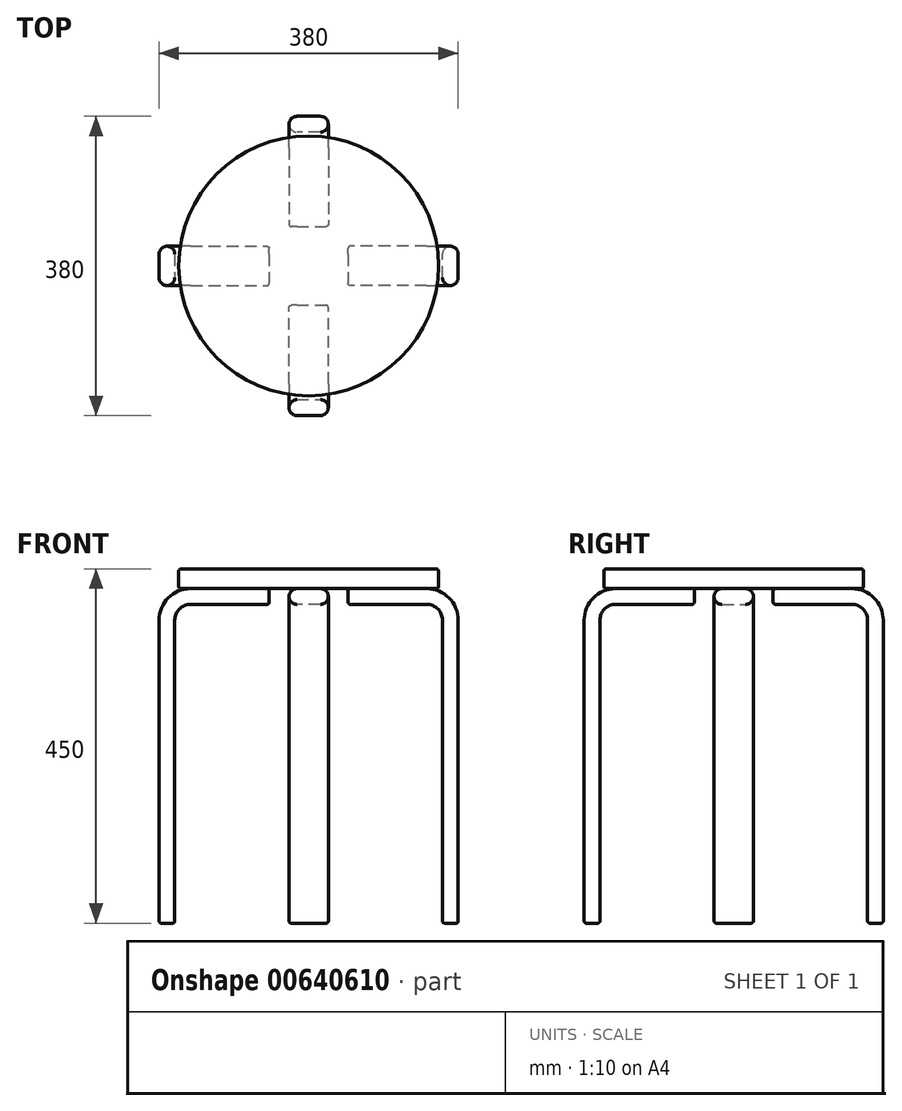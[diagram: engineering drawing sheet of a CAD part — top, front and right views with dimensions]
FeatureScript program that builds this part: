
annotation { "Feature Type Name" : "Feature", "Feature Type Description" : "" }
export const myFeature = defineFeature(function(context is Context, id is Id, definition is map)
    precondition{}
    {
        {
            var Q0;
            Q0=qCreatedBy(makeId("Top.planeOp"),FACE);
            var sketch = newSketch(context, id + "F0", { "sketchPlane" : qUnion([Q0])});
            skLineSegment(sketch, "E0", {"start": v(0, 0) * mm, "end": v(-180, 0) * mm, "construction": true});
            skLineSegment(sketch, "E1", {"start": v(-180, -15) * mm, "end": v(-180, 15) * mm, "construction": true});
            skArc(sketch, "E2", {"start": v(-170, 15) * mm, "mid": v(-180, 25) * mm, "end": v(-190, 15) * mm});
            skArc(sketch, "E3", {"start": v(-190, -15) * mm, "mid": v(-180, -25) * mm, "end": v(-170, -15) * mm});
            skLineSegment(sketch, "E4", {"start": v(-180, 15) * mm, "end": v(-170, 15) * mm, "construction": true});
            skLineSegment(sketch, "E5", {"start": v(-190, 15) * mm, "end": v(-190, -15) * mm});
            skLineSegment(sketch, "E6", {"start": v(-170, 15) * mm, "end": v(-170, -15) * mm});
            skSolve(sketch);
        }
        {
            var Q0;
            Q0=qCreatedBy(makeId("Front.planeOp"),FACE);
            var sketch = newSketch(context, id + "F1", { "sketchPlane" : qUnion([Q0])});
            skLineSegment(sketch, "E7", {"start": v(-180, 0) * mm, "end": v(-180, 385) * mm});
            skLineSegment(sketch, "E8", {"start": v(-50, 415) * mm, "end": v(-150, 415) * mm});
            skPoint(sketch, "E9.visualSharp", {"position": v(-180, 415) * mm});
            skArc(sketch, "E9.filletArc", {"start": v(-150, 415) * mm, "mid": v(-171.21, 406.21) * mm, "end": v(-180, 385) * mm});
            skSolve(sketch);
        }
        {
            var Q0;
            Q0=makeQuery(id+"F0.imprint","IMPRINT",FACE,{"disambiguationData":[TD([[makeQuery(id+"F0.imprint","IMPRINT",EDGE,{"derivedFrom":sQuery(id+"F0.wireOp",EDGE,"E2")}),1.0]])]});
            var Q1;
            Q1=sQuery(id+"F1.wireOp",EDGE,"E7");
            var Q2;
            Q2=sQuery(id+"F1.wireOp",EDGE,"E9.filletArc");
            var Q3;
            Q3=sQuery(id+"F1.wireOp",EDGE,"E8");
            sweep(context, id + "F2", {"profiles" : qUnion([Q0]), "path" : qUnion([Q1, Q2, Q3])});
        }
        {
            var Q0;
            Q0=qCreatedBy(makeId("Front.planeOp"),FACE);
            var sketch = newSketch(context, id + "F3", { "sketchPlane" : qUnion([Q0])});
            skLineSegment(sketch, "E10", {"start": v(0, 0) * mm, "end": v(0, 83.06) * mm, "construction": true});
            skSolve(sketch);
        }
        {
            var Q0;
            Q0=makeQuery(id+"F2.opSweep","SWEPT_BODY",BODY,{"disambiguationData":[OSD([sQuery(id+"F0.wireOp",EDGE,"E2"),sQuery(id+"F0.wireOp",EDGE,"E3"),sQuery(id+"F0.wireOp",EDGE,"E5"),sQuery(id+"F0.wireOp",EDGE,"E6"),sQuery(id+"F1.wireOp",EDGE,"E8")])]});
            var Q1;
            Q1=sQuery(id+"F3.wireOp",EDGE,"E10");
            circularPattern(context, id + "F4", {"entities" : qUnion([Q0]), "axis" : qUnion([Q1]), "angle" : 360 * degree, "instanceCount" : 4, "equalSpace" : true});
        }
        {
            var Q0;
            Q0=qCreatedBy(makeId("Front.planeOp"),FACE);
            var sketch = newSketch(context, id + "F5", { "sketchPlane" : qUnion([Q0])});
            skLineSegment(sketch, "E11.bottom", {"start": v(-165, 450) * mm, "end": v(0, 450) * mm});
            skLineSegment(sketch, "E11.top", {"start": v(-165, 425) * mm, "end": v(0, 425) * mm});
            skLineSegment(sketch, "E11.left", {"start": v(-165, 450) * mm, "end": v(-165, 425) * mm});
            skLineSegment(sketch, "E11.right", {"start": v(0, 450) * mm, "end": v(0, 425) * mm});
            skSolve(sketch);
        }
        {
            var Q0;
            Q0=makeQuery(id+"F5.imprint","IMPRINT",FACE,{"disambiguationData":[TD([[makeQuery(id+"F5.imprint","IMPRINT",EDGE,{"derivedFrom":sQuery(id+"F5.wireOp",EDGE,"E11.bottom")}),-1.0]])]});
            var Q1;
            Q1=sQuery(id+"F3.wireOp",EDGE,"E10");
            revolve(context, id + "F6", {"entities" : qUnion([Q0]), "axis" : qUnion([Q1]), "revolveType" : RevolveType.FULL});
        }
        {
            var Q0;
            Q0=makeQuery(id+"F6.opRevolve","SWEPT_FACE",FACE,{"disambiguationData":[OSD([sQuery(id+"F5.wireOp",EDGE,"E11.left")])]});
            var Q1;
            Q1=makeQuery(id+"F6.opRevolve","SWEPT_EDGE",EDGE,{"disambiguationData":[OSD([sQuery(id+"F5.wireOp",EDGE,"E11.top"),sQuery(id+"F5.wireOp",EDGE,"E11.left")])]});
            var Q2;
            Q2=makeQuery(id+"F6.opRevolve","SWEPT_EDGE",EDGE,{"disambiguationData":[OSD([sQuery(id+"F5.wireOp",EDGE,"E11.bottom"),sQuery(id+"F5.wireOp",EDGE,"E11.left")])]});
            var Q3;
            Q3=makeQuery(id+"F6.opRevolve","SWEPT_FACE",FACE,{"disambiguationData":[OSD([sQuery(id+"F5.wireOp",EDGE,"E11.top")])]});
            var Q4;
            Q4=makeQuery(id+"F6.opRevolve","SWEPT_FACE",FACE,{"disambiguationData":[OSD([sQuery(id+"F5.wireOp",EDGE,"E11.bottom")])]});
            var Q5;
            Q5=makeQuery(id+"F4.opPattern","COPY",FACE,{"derivedFrom":makeQuery(id+"F2.opSweep","SWEPT_FACE",FACE,{"disambiguationData":[OSD([sQuery(id+"F0.wireOp",EDGE,"E2"),sQuery(id+"F1.wireOp",EDGE,"E7")])]}),"instanceName":"3"});
            var Q6;
            Q6=makeQuery(id+"F4.opPattern","COPY",FACE,{"derivedFrom":makeQuery(id+"F2.opSweep","SWEPT_FACE",FACE,{"disambiguationData":[OSD([sQuery(id+"F0.wireOp",EDGE,"E3"),sQuery(id+"F1.wireOp",EDGE,"E7")])]}),"instanceName":"3"});
            var Q7;
            Q7=makeQuery(id+"F4.opPattern","COPY",FACE,{"derivedFrom":makeQuery(id+"F2.opSweep","SWEPT_FACE",FACE,{"disambiguationData":[OSD([sQuery(id+"F0.wireOp",EDGE,"E6"),sQuery(id+"F1.wireOp",EDGE,"E7")])]}),"instanceName":"3"});
            var Q8;
            Q8=makeQuery(id+"F4.opPattern","COPY",FACE,{"derivedFrom":makeQuery(id+"F2.opSweep","CAP_FACE",FACE,{"disambiguationData":[OSD([sQuery(id+"F0.wireOp",EDGE,"E2"),sQuery(id+"F0.wireOp",EDGE,"E3"),sQuery(id+"F0.wireOp",EDGE,"E5"),sQuery(id+"F0.wireOp",EDGE,"E6"),sQuery(id+"F1.wireOp",VERTEX,"E7.start")])],"isStart":true}),"instanceName":"3"});
            var Q9;
            Q9=makeQuery(id+"F4.opPattern","COPY",FACE,{"derivedFrom":makeQuery(id+"F2.opSweep","SWEPT_FACE",FACE,{"disambiguationData":[OSD([sQuery(id+"F0.wireOp",EDGE,"E5"),sQuery(id+"F1.wireOp",EDGE,"E7")])]}),"instanceName":"1"});
            var Q10;
            Q10=makeQuery(id+"F4.opPattern","COPY",FACE,{"derivedFrom":makeQuery(id+"F2.opSweep","SWEPT_FACE",FACE,{"disambiguationData":[OSD([sQuery(id+"F0.wireOp",EDGE,"E3"),sQuery(id+"F1.wireOp",EDGE,"E9.filletArc")])]}),"instanceName":"1"});
            var Q11;
            Q11=makeQuery(id+"F4.opPattern","COPY",FACE,{"derivedFrom":makeQuery(id+"F2.opSweep","SWEPT_FACE",FACE,{"disambiguationData":[OSD([sQuery(id+"F0.wireOp",EDGE,"E3"),sQuery(id+"F1.wireOp",EDGE,"E8")])]}),"instanceName":"1"});
            var Q12;
            Q12=makeQuery(id+"F4.opPattern","COPY",FACE,{"derivedFrom":makeQuery(id+"F2.opSweep","SWEPT_FACE",FACE,{"disambiguationData":[OSD([sQuery(id+"F0.wireOp",EDGE,"E3"),sQuery(id+"F1.wireOp",EDGE,"E7")])]}),"instanceName":"1"});
            var Q13;
            Q13=makeQuery(id+"F4.opPattern","COPY",FACE,{"derivedFrom":makeQuery(id+"F2.opSweep","SWEPT_FACE",FACE,{"disambiguationData":[OSD([sQuery(id+"F0.wireOp",EDGE,"E2"),sQuery(id+"F1.wireOp",EDGE,"E9.filletArc")])]}),"instanceName":"1"});
            var Q14;
            Q14=makeQuery(id+"F4.opPattern","COPY",FACE,{"derivedFrom":makeQuery(id+"F2.opSweep","SWEPT_FACE",FACE,{"disambiguationData":[OSD([sQuery(id+"F0.wireOp",EDGE,"E2"),sQuery(id+"F1.wireOp",EDGE,"E7")])]}),"instanceName":"1"});
            var Q15;
            Q15=makeQuery(id+"F4.opPattern","COPY",FACE,{"derivedFrom":makeQuery(id+"F2.opSweep","CAP_FACE",FACE,{"disambiguationData":[OSD([sQuery(id+"F0.wireOp",EDGE,"E2"),sQuery(id+"F0.wireOp",EDGE,"E3"),sQuery(id+"F0.wireOp",EDGE,"E5"),sQuery(id+"F0.wireOp",EDGE,"E6"),sQuery(id+"F1.wireOp",VERTEX,"E8.start")])],"isStart":false}),"instanceName":"1"});
            var Q16;
            Q16=makeQuery(id+"F4.opPattern","COPY",FACE,{"derivedFrom":makeQuery(id+"F2.opSweep","CAP_FACE",FACE,{"disambiguationData":[OSD([sQuery(id+"F0.wireOp",EDGE,"E2"),sQuery(id+"F0.wireOp",EDGE,"E3"),sQuery(id+"F0.wireOp",EDGE,"E5"),sQuery(id+"F0.wireOp",EDGE,"E6"),sQuery(id+"F1.wireOp",VERTEX,"E7.start")])],"isStart":true}),"instanceName":"1"});
            var Q17;
            Q17=makeQuery(id+"F4.opPattern","COPY",FACE,{"derivedFrom":makeQuery(id+"F2.opSweep","SWEPT_FACE",FACE,{"disambiguationData":[OSD([sQuery(id+"F0.wireOp",EDGE,"E5"),sQuery(id+"F1.wireOp",EDGE,"E9.filletArc")])]}),"instanceName":"1"});
            var Q18;
            Q18=makeQuery(id+"F4.opPattern","COPY",EDGE,{"derivedFrom":makeQuery(id+"F2.opSweep","CAP_EDGE",EDGE,{"disambiguationData":[OSD([sQuery(id+"F0.wireOp",EDGE,"E5"),sQuery(id+"F1.wireOp",VERTEX,"E7.start")])],"isStart":true}),"instanceName":"1"});
            var Q19;
            Q19=makeQuery(id+"F4.opPattern","COPY",FACE,{"derivedFrom":makeQuery(id+"F2.opSweep","CAP_FACE",FACE,{"disambiguationData":[OSD([sQuery(id+"F0.wireOp",EDGE,"E2"),sQuery(id+"F0.wireOp",EDGE,"E3"),sQuery(id+"F0.wireOp",EDGE,"E5"),sQuery(id+"F0.wireOp",EDGE,"E6"),sQuery(id+"F1.wireOp",VERTEX,"E8.start")])],"isStart":false}),"instanceName":"2"});
            var Q20;
            Q20=makeQuery(id+"F4.opPattern","COPY",FACE,{"derivedFrom":makeQuery(id+"F2.opSweep","CAP_FACE",FACE,{"disambiguationData":[OSD([sQuery(id+"F0.wireOp",EDGE,"E2"),sQuery(id+"F0.wireOp",EDGE,"E3"),sQuery(id+"F0.wireOp",EDGE,"E5"),sQuery(id+"F0.wireOp",EDGE,"E6"),sQuery(id+"F1.wireOp",VERTEX,"E7.start")])],"isStart":true}),"instanceName":"2"});
            var Q21;
            Q21=makeQuery(id+"F4.opPattern","COPY",FACE,{"derivedFrom":makeQuery(id+"F2.opSweep","SWEPT_FACE",FACE,{"disambiguationData":[OSD([sQuery(id+"F0.wireOp",EDGE,"E2"),sQuery(id+"F1.wireOp",EDGE,"E7")])]}),"instanceName":"2"});
            var Q22;
            Q22=makeQuery(id+"F4.opPattern","COPY",EDGE,{"derivedFrom":makeQuery(id+"F2.opSweep","SWEPT_EDGE",EDGE,{"disambiguationData":[OSD([sQuery(id+"F0.wireOp",EDGE,"E2"),sQuery(id+"F0.wireOp",EDGE,"E5"),sQuery(id+"F1.wireOp",EDGE,"E9.filletArc")])]}),"instanceName":"2"});
            var Q23;
            Q23=makeQuery(id+"F4.opPattern","COPY",FACE,{"derivedFrom":makeQuery(id+"F2.opSweep","SWEPT_FACE",FACE,{"disambiguationData":[OSD([sQuery(id+"F0.wireOp",EDGE,"E2"),sQuery(id+"F1.wireOp",EDGE,"E8")])]}),"instanceName":"2"});
            var Q24;
            Q24=makeQuery(id+"F4.opPattern","COPY",FACE,{"derivedFrom":makeQuery(id+"F2.opSweep","SWEPT_FACE",FACE,{"disambiguationData":[OSD([sQuery(id+"F0.wireOp",EDGE,"E2"),sQuery(id+"F1.wireOp",EDGE,"E9.filletArc")])]}),"instanceName":"2"});
            var Q25;
            Q25=makeQuery(id+"F4.opPattern","COPY",EDGE,{"derivedFrom":makeQuery(id+"F2.opSweep","MID_CAP_EDGE",EDGE,{"disambiguationData":[OSD([sQuery(id+"F0.wireOp",EDGE,"E5"),sQuery(id+"F1.wireOp",VERTEX,"E9.filletArc.end")])],"capPos":1.0}),"instanceName":"2"});
            var Q26;
            Q26=makeQuery(id+"F4.opPattern","COPY",FACE,{"derivedFrom":makeQuery(id+"F2.opSweep","SWEPT_FACE",FACE,{"disambiguationData":[OSD([sQuery(id+"F0.wireOp",EDGE,"E3"),sQuery(id+"F1.wireOp",EDGE,"E7")])]}),"instanceName":"2"});
            var Q27;
            Q27=makeQuery(id+"F4.opPattern","COPY",EDGE,{"derivedFrom":makeQuery(id+"F2.opSweep","SWEPT_EDGE",EDGE,{"disambiguationData":[OSD([sQuery(id+"F0.wireOp",EDGE,"E3"),sQuery(id+"F0.wireOp",EDGE,"E5"),sQuery(id+"F1.wireOp",EDGE,"E9.filletArc")])]}),"instanceName":"2"});
            var Q28;
            Q28=makeQuery(id+"F4.opPattern","COPY",FACE,{"derivedFrom":makeQuery(id+"F2.opSweep","SWEPT_FACE",FACE,{"disambiguationData":[OSD([sQuery(id+"F0.wireOp",EDGE,"E3"),sQuery(id+"F1.wireOp",EDGE,"E9.filletArc")])]}),"instanceName":"2"});
            var Q29;
            Q29=makeQuery(id+"F4.opPattern","COPY",FACE,{"derivedFrom":makeQuery(id+"F2.opSweep","SWEPT_FACE",FACE,{"disambiguationData":[OSD([sQuery(id+"F0.wireOp",EDGE,"E5"),sQuery(id+"F1.wireOp",EDGE,"E7")])]}),"instanceName":"2"});
            var Q30;
            Q30=makeQuery(id+"F4.opPattern","COPY",FACE,{"derivedFrom":makeQuery(id+"F2.opSweep","SWEPT_FACE",FACE,{"disambiguationData":[OSD([sQuery(id+"F0.wireOp",EDGE,"E5"),sQuery(id+"F1.wireOp",EDGE,"E9.filletArc")])]}),"instanceName":"2"});
            var Q31;
            Q31=makeQuery(id+"F2.opSweep","SWEPT_FACE",FACE,{"disambiguationData":[OSD([sQuery(id+"F0.wireOp",EDGE,"E3"),sQuery(id+"F1.wireOp",EDGE,"E8")])]});
            var Q32;
            Q32=makeQuery(id+"F2.opSweep","SWEPT_FACE",FACE,{"disambiguationData":[OSD([sQuery(id+"F0.wireOp",EDGE,"E2"),sQuery(id+"F1.wireOp",EDGE,"E7")])]});
            var Q33;
            Q33=makeQuery(id+"F2.opSweep","SWEPT_FACE",FACE,{"disambiguationData":[OSD([sQuery(id+"F0.wireOp",EDGE,"E3"),sQuery(id+"F1.wireOp",EDGE,"E9.filletArc")])]});
            var Q34;
            Q34=makeQuery(id+"F2.opSweep","CAP_FACE",FACE,{"disambiguationData":[OSD([sQuery(id+"F0.wireOp",EDGE,"E2"),sQuery(id+"F0.wireOp",EDGE,"E3"),sQuery(id+"F0.wireOp",EDGE,"E5"),sQuery(id+"F0.wireOp",EDGE,"E6"),sQuery(id+"F1.wireOp",VERTEX,"E7.start")])],"isStart":true});
            var Q35;
            Q35=makeQuery(id+"F2.opSweep","SWEPT_FACE",FACE,{"disambiguationData":[OSD([sQuery(id+"F0.wireOp",EDGE,"E3"),sQuery(id+"F1.wireOp",EDGE,"E7")])]});
            var Q36;
            Q36=makeQuery(id+"F2.opSweep","SWEPT_EDGE",EDGE,{"disambiguationData":[OSD([sQuery(id+"F0.wireOp",EDGE,"E2"),sQuery(id+"F0.wireOp",EDGE,"E6"),sQuery(id+"F1.wireOp",EDGE,"E7")])]});
            var Q37;
            Q37=makeQuery(id+"F2.opSweep","SWEPT_FACE",FACE,{"disambiguationData":[OSD([sQuery(id+"F0.wireOp",EDGE,"E6"),sQuery(id+"F1.wireOp",EDGE,"E9.filletArc")])]});
            var Q38;
            Q38=makeQuery(id+"F2.opSweep","SWEPT_EDGE",EDGE,{"disambiguationData":[OSD([sQuery(id+"F0.wireOp",EDGE,"E3"),sQuery(id+"F0.wireOp",EDGE,"E6"),sQuery(id+"F1.wireOp",EDGE,"E7")])]});
            var Q39;
            Q39=makeQuery(id+"F2.opSweep","SWEPT_FACE",FACE,{"disambiguationData":[OSD([sQuery(id+"F0.wireOp",EDGE,"E6"),sQuery(id+"F1.wireOp",EDGE,"E7")])]});
            var Q40;
            Q40=makeQuery(id+"F4.opPattern","COPY",FACE,{"derivedFrom":makeQuery(id+"F2.opSweep","SWEPT_FACE",FACE,{"disambiguationData":[OSD([sQuery(id+"F0.wireOp",EDGE,"E2"),sQuery(id+"F1.wireOp",EDGE,"E8")])]}),"instanceName":"3"});
            var Q41;
            Q41=makeQuery(id+"F4.opPattern","COPY",EDGE,{"derivedFrom":makeQuery(id+"F2.opSweep","CAP_EDGE",EDGE,{"disambiguationData":[OSD([sQuery(id+"F0.wireOp",EDGE,"E5"),sQuery(id+"F1.wireOp",VERTEX,"E8.start")])],"isStart":false}),"instanceName":"3"});
            var Q42;
            Q42=makeQuery(id+"F4.opPattern","COPY",FACE,{"derivedFrom":makeQuery(id+"F2.opSweep","CAP_FACE",FACE,{"disambiguationData":[OSD([sQuery(id+"F0.wireOp",EDGE,"E2"),sQuery(id+"F0.wireOp",EDGE,"E3"),sQuery(id+"F0.wireOp",EDGE,"E5"),sQuery(id+"F0.wireOp",EDGE,"E6"),sQuery(id+"F1.wireOp",VERTEX,"E8.start")])],"isStart":false}),"instanceName":"3"});
            var Q43;
            Q43=makeQuery(id+"F4.opPattern","COPY",EDGE,{"derivedFrom":makeQuery(id+"F2.opSweep","CAP_EDGE",EDGE,{"disambiguationData":[OSD([sQuery(id+"F0.wireOp",EDGE,"E6"),sQuery(id+"F1.wireOp",VERTEX,"E7.start")])],"isStart":true}),"instanceName":"3"});
            var Q44;
            Q44=makeQuery(id+"F4.opPattern","COPY",FACE,{"derivedFrom":makeQuery(id+"F2.opSweep","SWEPT_FACE",FACE,{"disambiguationData":[OSD([sQuery(id+"F0.wireOp",EDGE,"E2"),sQuery(id+"F1.wireOp",EDGE,"E9.filletArc")])]}),"instanceName":"3"});
            var Q45;
            Q45=makeQuery(id+"F4.opPattern","COPY",EDGE,{"derivedFrom":makeQuery(id+"F2.opSweep","SWEPT_EDGE",EDGE,{"disambiguationData":[OSD([sQuery(id+"F0.wireOp",EDGE,"E3"),sQuery(id+"F0.wireOp",EDGE,"E6"),sQuery(id+"F1.wireOp",EDGE,"E7")])]}),"instanceName":"3"});
            var Q46;
            Q46=makeQuery(id+"F4.opPattern","COPY",FACE,{"derivedFrom":makeQuery(id+"F2.opSweep","SWEPT_FACE",FACE,{"disambiguationData":[OSD([sQuery(id+"F0.wireOp",EDGE,"E3"),sQuery(id+"F1.wireOp",EDGE,"E8")])]}),"instanceName":"3"});
            var Q47;
            Q47=makeQuery(id+"F4.opPattern","COPY",EDGE,{"derivedFrom":makeQuery(id+"F2.opSweep","CAP_EDGE",EDGE,{"disambiguationData":[OSD([sQuery(id+"F0.wireOp",EDGE,"E2"),sQuery(id+"F1.wireOp",VERTEX,"E7.start")])],"isStart":true}),"instanceName":"3"});
            var Q48;
            Q48=makeQuery(id+"F4.opPattern","COPY",FACE,{"derivedFrom":makeQuery(id+"F2.opSweep","SWEPT_FACE",FACE,{"disambiguationData":[OSD([sQuery(id+"F0.wireOp",EDGE,"E5"),sQuery(id+"F1.wireOp",EDGE,"E7")])]}),"instanceName":"3"});
            var Q49;
            Q49=makeQuery(id+"F4.opPattern","COPY",FACE,{"derivedFrom":makeQuery(id+"F2.opSweep","SWEPT_FACE",FACE,{"disambiguationData":[OSD([sQuery(id+"F0.wireOp",EDGE,"E5"),sQuery(id+"F1.wireOp",EDGE,"E8")])]}),"instanceName":"3"});
            var Q50;
            Q50=makeQuery(id+"F4.opPattern","COPY",FACE,{"derivedFrom":makeQuery(id+"F2.opSweep","SWEPT_FACE",FACE,{"disambiguationData":[OSD([sQuery(id+"F0.wireOp",EDGE,"E5"),sQuery(id+"F1.wireOp",EDGE,"E9.filletArc")])]}),"instanceName":"3"});
            var Q51;
            Q51=makeQuery(id+"F4.opPattern","COPY",EDGE,{"derivedFrom":makeQuery(id+"F2.opSweep","SWEPT_EDGE",EDGE,{"disambiguationData":[OSD([sQuery(id+"F0.wireOp",EDGE,"E2"),sQuery(id+"F0.wireOp",EDGE,"E6"),sQuery(id+"F1.wireOp",EDGE,"E7")])]}),"instanceName":"3"});
            var Q52;
            Q52=makeQuery(id+"F4.opPattern","COPY",EDGE,{"derivedFrom":makeQuery(id+"F2.opSweep","CAP_EDGE",EDGE,{"disambiguationData":[OSD([sQuery(id+"F0.wireOp",EDGE,"E3"),sQuery(id+"F1.wireOp",VERTEX,"E7.start")])],"isStart":true}),"instanceName":"3"});
            var Q53;
            Q53=makeQuery(id+"F4.opPattern","COPY",FACE,{"derivedFrom":makeQuery(id+"F2.opSweep","SWEPT_FACE",FACE,{"disambiguationData":[OSD([sQuery(id+"F0.wireOp",EDGE,"E6"),sQuery(id+"F1.wireOp",EDGE,"E8")])]}),"instanceName":"3"});
            var Q54;
            Q54=makeQuery(id+"F4.opPattern","COPY",EDGE,{"derivedFrom":makeQuery(id+"F2.opSweep","CAP_EDGE",EDGE,{"disambiguationData":[OSD([sQuery(id+"F0.wireOp",EDGE,"E5"),sQuery(id+"F1.wireOp",VERTEX,"E7.start")])],"isStart":true}),"instanceName":"3"});
            var Q55;
            Q55=makeQuery(id+"F4.opPattern","COPY",EDGE,{"derivedFrom":makeQuery(id+"F2.opSweep","SWEPT_EDGE",EDGE,{"disambiguationData":[OSD([sQuery(id+"F0.wireOp",EDGE,"E3"),sQuery(id+"F0.wireOp",EDGE,"E5"),sQuery(id+"F1.wireOp",EDGE,"E9.filletArc")])]}),"instanceName":"1"});
            var Q56;
            Q56=makeQuery(id+"F4.opPattern","COPY",EDGE,{"derivedFrom":makeQuery(id+"F2.opSweep","SWEPT_EDGE",EDGE,{"disambiguationData":[OSD([sQuery(id+"F0.wireOp",EDGE,"E3"),sQuery(id+"F0.wireOp",EDGE,"E5"),sQuery(id+"F1.wireOp",EDGE,"E7")])]}),"instanceName":"1"});
            var Q57;
            Q57=makeQuery(id+"F4.opPattern","COPY",EDGE,{"derivedFrom":makeQuery(id+"F2.opSweep","SWEPT_EDGE",EDGE,{"disambiguationData":[OSD([sQuery(id+"F0.wireOp",EDGE,"E2"),sQuery(id+"F0.wireOp",EDGE,"E5"),sQuery(id+"F1.wireOp",EDGE,"E9.filletArc")])]}),"instanceName":"1"});
            var Q58;
            Q58=makeQuery(id+"F4.opPattern","COPY",FACE,{"derivedFrom":makeQuery(id+"F2.opSweep","SWEPT_FACE",FACE,{"disambiguationData":[OSD([sQuery(id+"F0.wireOp",EDGE,"E2"),sQuery(id+"F1.wireOp",EDGE,"E8")])]}),"instanceName":"1"});
            var Q59;
            Q59=makeQuery(id+"F4.opPattern","COPY",EDGE,{"derivedFrom":makeQuery(id+"F2.opSweep","SWEPT_EDGE",EDGE,{"disambiguationData":[OSD([sQuery(id+"F0.wireOp",EDGE,"E2"),sQuery(id+"F0.wireOp",EDGE,"E5"),sQuery(id+"F1.wireOp",EDGE,"E7")])]}),"instanceName":"1"});
            var Q60;
            Q60=makeQuery(id+"F4.opPattern","COPY",EDGE,{"derivedFrom":makeQuery(id+"F2.opSweep","SWEPT_EDGE",EDGE,{"disambiguationData":[OSD([sQuery(id+"F0.wireOp",EDGE,"E2"),sQuery(id+"F0.wireOp",EDGE,"E6"),sQuery(id+"F1.wireOp",EDGE,"E7")])]}),"instanceName":"1"});
            var Q61;
            Q61=makeQuery(id+"F4.opPattern","COPY",EDGE,{"derivedFrom":makeQuery(id+"F2.opSweep","MID_CAP_EDGE",EDGE,{"disambiguationData":[OSD([sQuery(id+"F0.wireOp",EDGE,"E2"),sQuery(id+"F1.wireOp",VERTEX,"E9.filletArc.end")])],"capPos":1.0}),"instanceName":"1"});
            var Q62;
            Q62=makeQuery(id+"F4.opPattern","COPY",FACE,{"derivedFrom":makeQuery(id+"F2.opSweep","SWEPT_FACE",FACE,{"disambiguationData":[OSD([sQuery(id+"F0.wireOp",EDGE,"E6"),sQuery(id+"F1.wireOp",EDGE,"E9.filletArc")])]}),"instanceName":"1"});
            var Q63;
            Q63=makeQuery(id+"F4.opPattern","COPY",EDGE,{"derivedFrom":makeQuery(id+"F2.opSweep","SWEPT_EDGE",EDGE,{"disambiguationData":[OSD([sQuery(id+"F0.wireOp",EDGE,"E3"),sQuery(id+"F0.wireOp",EDGE,"E6"),sQuery(id+"F1.wireOp",EDGE,"E7")])]}),"instanceName":"1"});
            var Q64;
            Q64=makeQuery(id+"F4.opPattern","COPY",FACE,{"derivedFrom":makeQuery(id+"F2.opSweep","SWEPT_FACE",FACE,{"disambiguationData":[OSD([sQuery(id+"F0.wireOp",EDGE,"E5"),sQuery(id+"F1.wireOp",EDGE,"E8")])]}),"instanceName":"1"});
            var Q65;
            Q65=makeQuery(id+"F4.opPattern","COPY",EDGE,{"derivedFrom":makeQuery(id+"F2.opSweep","SWEPT_EDGE",EDGE,{"disambiguationData":[OSD([sQuery(id+"F0.wireOp",EDGE,"E3"),sQuery(id+"F0.wireOp",EDGE,"E6"),sQuery(id+"F1.wireOp",EDGE,"E8")])]}),"instanceName":"1"});
            var Q66;
            Q66=makeQuery(id+"F4.opPattern","COPY",FACE,{"derivedFrom":makeQuery(id+"F2.opSweep","SWEPT_FACE",FACE,{"disambiguationData":[OSD([sQuery(id+"F0.wireOp",EDGE,"E6"),sQuery(id+"F1.wireOp",EDGE,"E7")])]}),"instanceName":"1"});
            var Q67;
            Q67=makeQuery(id+"F4.opPattern","COPY",EDGE,{"derivedFrom":makeQuery(id+"F2.opSweep","CAP_EDGE",EDGE,{"disambiguationData":[OSD([sQuery(id+"F0.wireOp",EDGE,"E2"),sQuery(id+"F1.wireOp",VERTEX,"E7.start")])],"isStart":true}),"instanceName":"1"});
            var Q68;
            Q68=makeQuery(id+"F4.opPattern","COPY",FACE,{"derivedFrom":makeQuery(id+"F2.opSweep","SWEPT_FACE",FACE,{"disambiguationData":[OSD([sQuery(id+"F0.wireOp",EDGE,"E6"),sQuery(id+"F1.wireOp",EDGE,"E8")])]}),"instanceName":"1"});
            var Q69;
            Q69=makeQuery(id+"F4.opPattern","COPY",EDGE,{"derivedFrom":makeQuery(id+"F2.opSweep","CAP_EDGE",EDGE,{"disambiguationData":[OSD([sQuery(id+"F0.wireOp",EDGE,"E3"),sQuery(id+"F1.wireOp",VERTEX,"E7.start")])],"isStart":true}),"instanceName":"1"});
            var Q70;
            Q70=makeQuery(id+"F4.opPattern","COPY",EDGE,{"derivedFrom":makeQuery(id+"F2.opSweep","CAP_EDGE",EDGE,{"disambiguationData":[OSD([sQuery(id+"F0.wireOp",EDGE,"E3"),sQuery(id+"F1.wireOp",VERTEX,"E8.start")])],"isStart":false}),"instanceName":"1"});
            var Q71;
            Q71=makeQuery(id+"F4.opPattern","COPY",EDGE,{"derivedFrom":makeQuery(id+"F2.opSweep","MID_CAP_EDGE",EDGE,{"disambiguationData":[OSD([sQuery(id+"F0.wireOp",EDGE,"E3"),sQuery(id+"F1.wireOp",VERTEX,"E8.end")])],"capPos":2.0}),"instanceName":"1"});
            var Q72;
            Q72=makeQuery(id+"F4.opPattern","COPY",EDGE,{"derivedFrom":makeQuery(id+"F2.opSweep","MID_CAP_EDGE",EDGE,{"disambiguationData":[OSD([sQuery(id+"F0.wireOp",EDGE,"E3"),sQuery(id+"F1.wireOp",VERTEX,"E9.filletArc.end")])],"capPos":1.0}),"instanceName":"1"});
            var Q73;
            Q73=makeQuery(id+"F4.opPattern","COPY",EDGE,{"derivedFrom":makeQuery(id+"F2.opSweep","CAP_EDGE",EDGE,{"disambiguationData":[OSD([sQuery(id+"F0.wireOp",EDGE,"E5"),sQuery(id+"F1.wireOp",VERTEX,"E8.start")])],"isStart":false}),"instanceName":"1"});
            var Q74;
            Q74=makeQuery(id+"F4.opPattern","COPY",EDGE,{"derivedFrom":makeQuery(id+"F2.opSweep","MID_CAP_EDGE",EDGE,{"disambiguationData":[OSD([sQuery(id+"F0.wireOp",EDGE,"E5"),sQuery(id+"F1.wireOp",VERTEX,"E8.end")])],"capPos":2.0}),"instanceName":"1"});
            var Q75;
            Q75=makeQuery(id+"F4.opPattern","COPY",EDGE,{"derivedFrom":makeQuery(id+"F2.opSweep","MID_CAP_EDGE",EDGE,{"disambiguationData":[OSD([sQuery(id+"F0.wireOp",EDGE,"E5"),sQuery(id+"F1.wireOp",VERTEX,"E9.filletArc.end")])],"capPos":1.0}),"instanceName":"1"});
            var Q76;
            Q76=makeQuery(id+"F4.opPattern","COPY",EDGE,{"derivedFrom":makeQuery(id+"F2.opSweep","SWEPT_EDGE",EDGE,{"disambiguationData":[OSD([sQuery(id+"F0.wireOp",EDGE,"E2"),sQuery(id+"F0.wireOp",EDGE,"E6"),sQuery(id+"F1.wireOp",EDGE,"E8")])]}),"instanceName":"2"});
            var Q77;
            Q77=makeQuery(id+"F4.opPattern","COPY",EDGE,{"derivedFrom":makeQuery(id+"F2.opSweep","SWEPT_EDGE",EDGE,{"disambiguationData":[OSD([sQuery(id+"F0.wireOp",EDGE,"E2"),sQuery(id+"F0.wireOp",EDGE,"E5"),sQuery(id+"F1.wireOp",EDGE,"E7")])]}),"instanceName":"2"});
            var Q78;
            Q78=makeQuery(id+"F4.opPattern","COPY",EDGE,{"derivedFrom":makeQuery(id+"F2.opSweep","MID_CAP_EDGE",EDGE,{"disambiguationData":[OSD([sQuery(id+"F0.wireOp",EDGE,"E3"),sQuery(id+"F1.wireOp",VERTEX,"E9.filletArc.end")])],"capPos":1.0}),"instanceName":"2"});
            var Q79;
            Q79=makeQuery(id+"F4.opPattern","COPY",EDGE,{"derivedFrom":makeQuery(id+"F2.opSweep","CAP_EDGE",EDGE,{"disambiguationData":[OSD([sQuery(id+"F0.wireOp",EDGE,"E5"),sQuery(id+"F1.wireOp",VERTEX,"E7.start")])],"isStart":true}),"instanceName":"2"});
            var Q80;
            Q80=makeQuery(id+"F4.opPattern","COPY",EDGE,{"derivedFrom":makeQuery(id+"F2.opSweep","CAP_EDGE",EDGE,{"disambiguationData":[OSD([sQuery(id+"F0.wireOp",EDGE,"E5"),sQuery(id+"F1.wireOp",VERTEX,"E8.start")])],"isStart":false}),"instanceName":"2"});
            var Q81;
            Q81=makeQuery(id+"F4.opPattern","COPY",EDGE,{"derivedFrom":makeQuery(id+"F2.opSweep","SWEPT_EDGE",EDGE,{"disambiguationData":[OSD([sQuery(id+"F0.wireOp",EDGE,"E3"),sQuery(id+"F0.wireOp",EDGE,"E5"),sQuery(id+"F1.wireOp",EDGE,"E7")])]}),"instanceName":"2"});
            var Q82;
            Q82=makeQuery(id+"F4.opPattern","COPY",FACE,{"derivedFrom":makeQuery(id+"F2.opSweep","SWEPT_FACE",FACE,{"disambiguationData":[OSD([sQuery(id+"F0.wireOp",EDGE,"E3"),sQuery(id+"F1.wireOp",EDGE,"E8")])]}),"instanceName":"2"});
            var Q83;
            Q83=makeQuery(id+"F4.opPattern","COPY",EDGE,{"derivedFrom":makeQuery(id+"F2.opSweep","SWEPT_EDGE",EDGE,{"disambiguationData":[OSD([sQuery(id+"F0.wireOp",EDGE,"E3"),sQuery(id+"F0.wireOp",EDGE,"E6"),sQuery(id+"F1.wireOp",EDGE,"E7")])]}),"instanceName":"2"});
            var Q84;
            Q84=makeQuery(id+"F4.opPattern","COPY",FACE,{"derivedFrom":makeQuery(id+"F2.opSweep","SWEPT_FACE",FACE,{"disambiguationData":[OSD([sQuery(id+"F0.wireOp",EDGE,"E5"),sQuery(id+"F1.wireOp",EDGE,"E8")])]}),"instanceName":"2"});
            var Q85;
            Q85=makeQuery(id+"F4.opPattern","COPY",EDGE,{"derivedFrom":makeQuery(id+"F2.opSweep","CAP_EDGE",EDGE,{"disambiguationData":[OSD([sQuery(id+"F0.wireOp",EDGE,"E2"),sQuery(id+"F1.wireOp",VERTEX,"E7.start")])],"isStart":true}),"instanceName":"2"});
            var Q86;
            Q86=makeQuery(id+"F4.opPattern","COPY",EDGE,{"derivedFrom":makeQuery(id+"F2.opSweep","CAP_EDGE",EDGE,{"disambiguationData":[OSD([sQuery(id+"F0.wireOp",EDGE,"E2"),sQuery(id+"F1.wireOp",VERTEX,"E8.start")])],"isStart":false}),"instanceName":"2"});
            var Q87;
            Q87=makeQuery(id+"F4.opPattern","COPY",FACE,{"derivedFrom":makeQuery(id+"F2.opSweep","SWEPT_FACE",FACE,{"disambiguationData":[OSD([sQuery(id+"F0.wireOp",EDGE,"E6"),sQuery(id+"F1.wireOp",EDGE,"E7")])]}),"instanceName":"2"});
            var Q88;
            Q88=makeQuery(id+"F4.opPattern","COPY",EDGE,{"derivedFrom":makeQuery(id+"F2.opSweep","MID_CAP_EDGE",EDGE,{"disambiguationData":[OSD([sQuery(id+"F0.wireOp",EDGE,"E2"),sQuery(id+"F1.wireOp",VERTEX,"E8.end")])],"capPos":2.0}),"instanceName":"2"});
            var Q89;
            Q89=makeQuery(id+"F4.opPattern","COPY",FACE,{"derivedFrom":makeQuery(id+"F2.opSweep","SWEPT_FACE",FACE,{"disambiguationData":[OSD([sQuery(id+"F0.wireOp",EDGE,"E6"),sQuery(id+"F1.wireOp",EDGE,"E8")])]}),"instanceName":"2"});
            var Q90;
            Q90=makeQuery(id+"F4.opPattern","COPY",EDGE,{"derivedFrom":makeQuery(id+"F2.opSweep","MID_CAP_EDGE",EDGE,{"disambiguationData":[OSD([sQuery(id+"F0.wireOp",EDGE,"E2"),sQuery(id+"F1.wireOp",VERTEX,"E9.filletArc.end")])],"capPos":1.0}),"instanceName":"2"});
            var Q91;
            Q91=makeQuery(id+"F4.opPattern","COPY",FACE,{"derivedFrom":makeQuery(id+"F2.opSweep","SWEPT_FACE",FACE,{"disambiguationData":[OSD([sQuery(id+"F0.wireOp",EDGE,"E6"),sQuery(id+"F1.wireOp",EDGE,"E9.filletArc")])]}),"instanceName":"2"});
            var Q92;
            Q92=makeQuery(id+"F4.opPattern","COPY",EDGE,{"derivedFrom":makeQuery(id+"F2.opSweep","SWEPT_EDGE",EDGE,{"disambiguationData":[OSD([sQuery(id+"F0.wireOp",EDGE,"E2"),sQuery(id+"F0.wireOp",EDGE,"E6"),sQuery(id+"F1.wireOp",EDGE,"E7")])]}),"instanceName":"2"});
            var Q93;
            Q93=makeQuery(id+"F4.opPattern","COPY",EDGE,{"derivedFrom":makeQuery(id+"F2.opSweep","CAP_EDGE",EDGE,{"disambiguationData":[OSD([sQuery(id+"F0.wireOp",EDGE,"E3"),sQuery(id+"F1.wireOp",VERTEX,"E7.start")])],"isStart":true}),"instanceName":"2"});
            var Q94;
            Q94=makeQuery(id+"F2.opSweep","SWEPT_FACE",FACE,{"disambiguationData":[OSD([sQuery(id+"F0.wireOp",EDGE,"E2"),sQuery(id+"F1.wireOp",EDGE,"E8")])]});
            var Q95;
            Q95=makeQuery(id+"F2.opSweep","SWEPT_FACE",FACE,{"disambiguationData":[OSD([sQuery(id+"F0.wireOp",EDGE,"E2"),sQuery(id+"F1.wireOp",EDGE,"E9.filletArc")])]});
            var Q96;
            Q96=makeQuery(id+"F2.opSweep","CAP_FACE",FACE,{"disambiguationData":[OSD([sQuery(id+"F0.wireOp",EDGE,"E2"),sQuery(id+"F0.wireOp",EDGE,"E3"),sQuery(id+"F0.wireOp",EDGE,"E5"),sQuery(id+"F0.wireOp",EDGE,"E6"),sQuery(id+"F1.wireOp",VERTEX,"E8.start")])],"isStart":false});
            var Q97;
            Q97=makeQuery(id+"F2.opSweep","SWEPT_EDGE",EDGE,{"disambiguationData":[OSD([sQuery(id+"F0.wireOp",EDGE,"E3"),sQuery(id+"F0.wireOp",EDGE,"E5"),sQuery(id+"F1.wireOp",EDGE,"E9.filletArc")])]});
            var Q98;
            Q98=makeQuery(id+"F2.opSweep","SWEPT_FACE",FACE,{"disambiguationData":[OSD([sQuery(id+"F0.wireOp",EDGE,"E5"),sQuery(id+"F1.wireOp",EDGE,"E7")])]});
            var Q99;
            Q99=makeQuery(id+"F2.opSweep","SWEPT_FACE",FACE,{"disambiguationData":[OSD([sQuery(id+"F0.wireOp",EDGE,"E5"),sQuery(id+"F1.wireOp",EDGE,"E8")])]});
            var Q100;
            Q100=makeQuery(id+"F2.opSweep","SWEPT_EDGE",EDGE,{"disambiguationData":[OSD([sQuery(id+"F0.wireOp",EDGE,"E3"),sQuery(id+"F0.wireOp",EDGE,"E6"),sQuery(id+"F1.wireOp",EDGE,"E8")])]});
            var Q101;
            Q101=makeQuery(id+"F2.opSweep","SWEPT_FACE",FACE,{"disambiguationData":[OSD([sQuery(id+"F0.wireOp",EDGE,"E5"),sQuery(id+"F1.wireOp",EDGE,"E9.filletArc")])]});
            var Q102;
            Q102=makeQuery(id+"F2.opSweep","SWEPT_EDGE",EDGE,{"disambiguationData":[OSD([sQuery(id+"F0.wireOp",EDGE,"E3"),sQuery(id+"F0.wireOp",EDGE,"E6"),sQuery(id+"F1.wireOp",EDGE,"E9.filletArc")])]});
            var Q103;
            Q103=makeQuery(id+"F2.opSweep","CAP_EDGE",EDGE,{"disambiguationData":[OSD([sQuery(id+"F0.wireOp",EDGE,"E2"),sQuery(id+"F1.wireOp",VERTEX,"E7.start")])],"isStart":true});
            var Q104;
            Q104=makeQuery(id+"F2.opSweep","SWEPT_FACE",FACE,{"disambiguationData":[OSD([sQuery(id+"F0.wireOp",EDGE,"E6"),sQuery(id+"F1.wireOp",EDGE,"E8")])]});
            var Q105;
            Q105=makeQuery(id+"F2.opSweep","CAP_EDGE",EDGE,{"disambiguationData":[OSD([sQuery(id+"F0.wireOp",EDGE,"E3"),sQuery(id+"F1.wireOp",VERTEX,"E7.start")])],"isStart":true});
            var Q106;
            Q106=makeQuery(id+"F2.opSweep","MID_CAP_EDGE",EDGE,{"disambiguationData":[OSD([sQuery(id+"F0.wireOp",EDGE,"E3"),sQuery(id+"F1.wireOp",VERTEX,"E8.end")])],"capPos":2.0});
            var Q107;
            Q107=makeQuery(id+"F2.opSweep","MID_CAP_EDGE",EDGE,{"disambiguationData":[OSD([sQuery(id+"F0.wireOp",EDGE,"E3"),sQuery(id+"F1.wireOp",VERTEX,"E9.filletArc.end")])],"capPos":1.0});
            var Q108;
            Q108=makeQuery(id+"F2.opSweep","CAP_EDGE",EDGE,{"disambiguationData":[OSD([sQuery(id+"F0.wireOp",EDGE,"E5"),sQuery(id+"F1.wireOp",VERTEX,"E7.start")])],"isStart":true});
            var Q109;
            Q109=makeQuery(id+"F2.opSweep","CAP_EDGE",EDGE,{"disambiguationData":[OSD([sQuery(id+"F0.wireOp",EDGE,"E6"),sQuery(id+"F1.wireOp",VERTEX,"E7.start")])],"isStart":true});
            var Q110;
            Q110=makeQuery(id+"F2.opSweep","MID_CAP_EDGE",EDGE,{"disambiguationData":[OSD([sQuery(id+"F0.wireOp",EDGE,"E6"),sQuery(id+"F1.wireOp",VERTEX,"E9.filletArc.end")])],"capPos":1.0});
            var Q111;
            Q111=makeQuery(id+"F4.opPattern","COPY",EDGE,{"derivedFrom":makeQuery(id+"F2.opSweep","SWEPT_EDGE",EDGE,{"disambiguationData":[OSD([sQuery(id+"F0.wireOp",EDGE,"E2"),sQuery(id+"F0.wireOp",EDGE,"E5"),sQuery(id+"F1.wireOp",EDGE,"E9.filletArc")])]}),"instanceName":"3"});
            var Q112;
            Q112=makeQuery(id+"F4.opPattern","COPY",EDGE,{"derivedFrom":makeQuery(id+"F2.opSweep","SWEPT_EDGE",EDGE,{"disambiguationData":[OSD([sQuery(id+"F0.wireOp",EDGE,"E3"),sQuery(id+"F0.wireOp",EDGE,"E5"),sQuery(id+"F1.wireOp",EDGE,"E7")])]}),"instanceName":"3"});
            var Q113;
            Q113=makeQuery(id+"F4.opPattern","COPY",EDGE,{"derivedFrom":makeQuery(id+"F2.opSweep","MID_CAP_EDGE",EDGE,{"disambiguationData":[OSD([sQuery(id+"F0.wireOp",EDGE,"E5"),sQuery(id+"F1.wireOp",VERTEX,"E8.end")])],"capPos":2.0}),"instanceName":"3"});
            var Q114;
            Q114=makeQuery(id+"F4.opPattern","COPY",EDGE,{"derivedFrom":makeQuery(id+"F2.opSweep","SWEPT_EDGE",EDGE,{"disambiguationData":[OSD([sQuery(id+"F0.wireOp",EDGE,"E3"),sQuery(id+"F0.wireOp",EDGE,"E5"),sQuery(id+"F1.wireOp",EDGE,"E8")])]}),"instanceName":"3"});
            var Q115;
            Q115=makeQuery(id+"F4.opPattern","COPY",EDGE,{"derivedFrom":makeQuery(id+"F2.opSweep","CAP_EDGE",EDGE,{"disambiguationData":[OSD([sQuery(id+"F0.wireOp",EDGE,"E6"),sQuery(id+"F1.wireOp",VERTEX,"E8.start")])],"isStart":false}),"instanceName":"3"});
            var Q116;
            Q116=makeQuery(id+"F4.opPattern","COPY",EDGE,{"derivedFrom":makeQuery(id+"F2.opSweep","SWEPT_EDGE",EDGE,{"disambiguationData":[OSD([sQuery(id+"F0.wireOp",EDGE,"E3"),sQuery(id+"F0.wireOp",EDGE,"E6"),sQuery(id+"F1.wireOp",EDGE,"E8")])]}),"instanceName":"3"});
            var Q117;
            Q117=makeQuery(id+"F4.opPattern","COPY",FACE,{"derivedFrom":makeQuery(id+"F2.opSweep","SWEPT_FACE",FACE,{"disambiguationData":[OSD([sQuery(id+"F0.wireOp",EDGE,"E3"),sQuery(id+"F1.wireOp",EDGE,"E9.filletArc")])]}),"instanceName":"3"});
            var Q118;
            Q118=makeQuery(id+"F4.opPattern","COPY",EDGE,{"derivedFrom":makeQuery(id+"F2.opSweep","CAP_EDGE",EDGE,{"disambiguationData":[OSD([sQuery(id+"F0.wireOp",EDGE,"E2"),sQuery(id+"F1.wireOp",VERTEX,"E8.start")])],"isStart":false}),"instanceName":"3"});
            var Q119;
            Q119=makeQuery(id+"F4.opPattern","COPY",EDGE,{"derivedFrom":makeQuery(id+"F2.opSweep","MID_CAP_EDGE",EDGE,{"disambiguationData":[OSD([sQuery(id+"F0.wireOp",EDGE,"E2"),sQuery(id+"F1.wireOp",VERTEX,"E8.end")])],"capPos":2.0}),"instanceName":"3"});
            var Q120;
            Q120=makeQuery(id+"F4.opPattern","COPY",EDGE,{"derivedFrom":makeQuery(id+"F2.opSweep","MID_CAP_EDGE",EDGE,{"disambiguationData":[OSD([sQuery(id+"F0.wireOp",EDGE,"E2"),sQuery(id+"F1.wireOp",VERTEX,"E9.filletArc.end")])],"capPos":1.0}),"instanceName":"3"});
            var Q121;
            Q121=makeQuery(id+"F4.opPattern","COPY",EDGE,{"derivedFrom":makeQuery(id+"F2.opSweep","SWEPT_EDGE",EDGE,{"disambiguationData":[OSD([sQuery(id+"F0.wireOp",EDGE,"E2"),sQuery(id+"F0.wireOp",EDGE,"E6"),sQuery(id+"F1.wireOp",EDGE,"E8")])]}),"instanceName":"3"});
            var Q122;
            Q122=makeQuery(id+"F4.opPattern","COPY",EDGE,{"derivedFrom":makeQuery(id+"F2.opSweep","CAP_EDGE",EDGE,{"disambiguationData":[OSD([sQuery(id+"F0.wireOp",EDGE,"E3"),sQuery(id+"F1.wireOp",VERTEX,"E8.start")])],"isStart":false}),"instanceName":"3"});
            var Q123;
            Q123=makeQuery(id+"F4.opPattern","COPY",FACE,{"derivedFrom":makeQuery(id+"F2.opSweep","SWEPT_FACE",FACE,{"disambiguationData":[OSD([sQuery(id+"F0.wireOp",EDGE,"E6"),sQuery(id+"F1.wireOp",EDGE,"E9.filletArc")])]}),"instanceName":"3"});
            var Q124;
            Q124=makeQuery(id+"F4.opPattern","COPY",EDGE,{"derivedFrom":makeQuery(id+"F2.opSweep","SWEPT_EDGE",EDGE,{"disambiguationData":[OSD([sQuery(id+"F0.wireOp",EDGE,"E2"),sQuery(id+"F0.wireOp",EDGE,"E5"),sQuery(id+"F1.wireOp",EDGE,"E7")])]}),"instanceName":"3"});
            var Q125;
            Q125=makeQuery(id+"F4.opPattern","COPY",EDGE,{"derivedFrom":makeQuery(id+"F2.opSweep","SWEPT_EDGE",EDGE,{"disambiguationData":[OSD([sQuery(id+"F0.wireOp",EDGE,"E2"),sQuery(id+"F0.wireOp",EDGE,"E5"),sQuery(id+"F1.wireOp",EDGE,"E8")])]}),"instanceName":"3"});
            var Q126;
            Q126=makeQuery(id+"F4.opPattern","COPY",EDGE,{"derivedFrom":makeQuery(id+"F2.opSweep","CAP_EDGE",EDGE,{"disambiguationData":[OSD([sQuery(id+"F0.wireOp",EDGE,"E2"),sQuery(id+"F1.wireOp",VERTEX,"E8.start")])],"isStart":false}),"instanceName":"1"});
            var Q127;
            Q127=makeQuery(id+"F4.opPattern","COPY",EDGE,{"derivedFrom":makeQuery(id+"F2.opSweep","SWEPT_EDGE",EDGE,{"disambiguationData":[OSD([sQuery(id+"F0.wireOp",EDGE,"E3"),sQuery(id+"F0.wireOp",EDGE,"E5"),sQuery(id+"F1.wireOp",EDGE,"E8")])]}),"instanceName":"1"});
            var Q128;
            Q128=makeQuery(id+"F4.opPattern","COPY",EDGE,{"derivedFrom":makeQuery(id+"F2.opSweep","SWEPT_EDGE",EDGE,{"disambiguationData":[OSD([sQuery(id+"F0.wireOp",EDGE,"E2"),sQuery(id+"F0.wireOp",EDGE,"E5"),sQuery(id+"F1.wireOp",EDGE,"E8")])]}),"instanceName":"1"});
            var Q129;
            Q129=makeQuery(id+"F4.opPattern","COPY",EDGE,{"derivedFrom":makeQuery(id+"F2.opSweep","SWEPT_EDGE",EDGE,{"disambiguationData":[OSD([sQuery(id+"F0.wireOp",EDGE,"E2"),sQuery(id+"F0.wireOp",EDGE,"E6"),sQuery(id+"F1.wireOp",EDGE,"E9.filletArc")])]}),"instanceName":"1"});
            var Q130;
            Q130=makeQuery(id+"F4.opPattern","COPY",EDGE,{"derivedFrom":makeQuery(id+"F2.opSweep","SWEPT_EDGE",EDGE,{"disambiguationData":[OSD([sQuery(id+"F0.wireOp",EDGE,"E2"),sQuery(id+"F0.wireOp",EDGE,"E6"),sQuery(id+"F1.wireOp",EDGE,"E8")])]}),"instanceName":"1"});
            var Q131;
            Q131=makeQuery(id+"F4.opPattern","COPY",EDGE,{"derivedFrom":makeQuery(id+"F2.opSweep","MID_CAP_EDGE",EDGE,{"disambiguationData":[OSD([sQuery(id+"F0.wireOp",EDGE,"E2"),sQuery(id+"F1.wireOp",VERTEX,"E8.end")])],"capPos":2.0}),"instanceName":"1"});
            var Q132;
            Q132=makeQuery(id+"F4.opPattern","COPY",EDGE,{"derivedFrom":makeQuery(id+"F2.opSweep","SWEPT_EDGE",EDGE,{"disambiguationData":[OSD([sQuery(id+"F0.wireOp",EDGE,"E3"),sQuery(id+"F0.wireOp",EDGE,"E6"),sQuery(id+"F1.wireOp",EDGE,"E9.filletArc")])]}),"instanceName":"1"});
            var Q133;
            Q133=makeQuery(id+"F4.opPattern","COPY",EDGE,{"derivedFrom":makeQuery(id+"F2.opSweep","CAP_EDGE",EDGE,{"disambiguationData":[OSD([sQuery(id+"F0.wireOp",EDGE,"E6"),sQuery(id+"F1.wireOp",VERTEX,"E7.start")])],"isStart":true}),"instanceName":"1"});
            var Q134;
            Q134=makeQuery(id+"F4.opPattern","COPY",EDGE,{"derivedFrom":makeQuery(id+"F2.opSweep","CAP_EDGE",EDGE,{"disambiguationData":[OSD([sQuery(id+"F0.wireOp",EDGE,"E6"),sQuery(id+"F1.wireOp",VERTEX,"E8.start")])],"isStart":false}),"instanceName":"1"});
            var Q135;
            Q135=makeQuery(id+"F4.opPattern","COPY",EDGE,{"derivedFrom":makeQuery(id+"F2.opSweep","MID_CAP_EDGE",EDGE,{"disambiguationData":[OSD([sQuery(id+"F0.wireOp",EDGE,"E6"),sQuery(id+"F1.wireOp",VERTEX,"E8.end")])],"capPos":2.0}),"instanceName":"1"});
            var Q136;
            Q136=makeQuery(id+"F4.opPattern","COPY",EDGE,{"derivedFrom":makeQuery(id+"F2.opSweep","MID_CAP_EDGE",EDGE,{"disambiguationData":[OSD([sQuery(id+"F0.wireOp",EDGE,"E6"),sQuery(id+"F1.wireOp",VERTEX,"E9.filletArc.end")])],"capPos":1.0}),"instanceName":"1"});
            var Q137;
            Q137=makeQuery(id+"F4.opPattern","COPY",EDGE,{"derivedFrom":makeQuery(id+"F2.opSweep","CAP_EDGE",EDGE,{"disambiguationData":[OSD([sQuery(id+"F0.wireOp",EDGE,"E3"),sQuery(id+"F1.wireOp",VERTEX,"E8.start")])],"isStart":false}),"instanceName":"2"});
            var Q138;
            Q138=makeQuery(id+"F4.opPattern","COPY",EDGE,{"derivedFrom":makeQuery(id+"F2.opSweep","SWEPT_EDGE",EDGE,{"disambiguationData":[OSD([sQuery(id+"F0.wireOp",EDGE,"E2"),sQuery(id+"F0.wireOp",EDGE,"E6"),sQuery(id+"F1.wireOp",EDGE,"E9.filletArc")])]}),"instanceName":"2"});
            var Q139;
            Q139=makeQuery(id+"F4.opPattern","COPY",EDGE,{"derivedFrom":makeQuery(id+"F2.opSweep","MID_CAP_EDGE",EDGE,{"disambiguationData":[OSD([sQuery(id+"F0.wireOp",EDGE,"E3"),sQuery(id+"F1.wireOp",VERTEX,"E8.end")])],"capPos":2.0}),"instanceName":"2"});
            var Q140;
            Q140=makeQuery(id+"F4.opPattern","COPY",EDGE,{"derivedFrom":makeQuery(id+"F2.opSweep","SWEPT_EDGE",EDGE,{"disambiguationData":[OSD([sQuery(id+"F0.wireOp",EDGE,"E2"),sQuery(id+"F0.wireOp",EDGE,"E5"),sQuery(id+"F1.wireOp",EDGE,"E8")])]}),"instanceName":"2"});
            var Q141;
            Q141=makeQuery(id+"F4.opPattern","COPY",EDGE,{"derivedFrom":makeQuery(id+"F2.opSweep","MID_CAP_EDGE",EDGE,{"disambiguationData":[OSD([sQuery(id+"F0.wireOp",EDGE,"E5"),sQuery(id+"F1.wireOp",VERTEX,"E8.end")])],"capPos":2.0}),"instanceName":"2"});
            var Q142;
            Q142=makeQuery(id+"F4.opPattern","COPY",EDGE,{"derivedFrom":makeQuery(id+"F2.opSweep","SWEPT_EDGE",EDGE,{"disambiguationData":[OSD([sQuery(id+"F0.wireOp",EDGE,"E3"),sQuery(id+"F0.wireOp",EDGE,"E5"),sQuery(id+"F1.wireOp",EDGE,"E8")])]}),"instanceName":"2"});
            var Q143;
            Q143=makeQuery(id+"F4.opPattern","COPY",EDGE,{"derivedFrom":makeQuery(id+"F2.opSweep","CAP_EDGE",EDGE,{"disambiguationData":[OSD([sQuery(id+"F0.wireOp",EDGE,"E6"),sQuery(id+"F1.wireOp",VERTEX,"E7.start")])],"isStart":true}),"instanceName":"2"});
            var Q144;
            Q144=makeQuery(id+"F4.opPattern","COPY",EDGE,{"derivedFrom":makeQuery(id+"F2.opSweep","CAP_EDGE",EDGE,{"disambiguationData":[OSD([sQuery(id+"F0.wireOp",EDGE,"E6"),sQuery(id+"F1.wireOp",VERTEX,"E8.start")])],"isStart":false}),"instanceName":"2"});
            var Q145;
            Q145=makeQuery(id+"F4.opPattern","COPY",EDGE,{"derivedFrom":makeQuery(id+"F2.opSweep","SWEPT_EDGE",EDGE,{"disambiguationData":[OSD([sQuery(id+"F0.wireOp",EDGE,"E3"),sQuery(id+"F0.wireOp",EDGE,"E6"),sQuery(id+"F1.wireOp",EDGE,"E8")])]}),"instanceName":"2"});
            var Q146;
            Q146=makeQuery(id+"F4.opPattern","COPY",EDGE,{"derivedFrom":makeQuery(id+"F2.opSweep","MID_CAP_EDGE",EDGE,{"disambiguationData":[OSD([sQuery(id+"F0.wireOp",EDGE,"E6"),sQuery(id+"F1.wireOp",VERTEX,"E8.end")])],"capPos":2.0}),"instanceName":"2"});
            var Q147;
            Q147=makeQuery(id+"F4.opPattern","COPY",EDGE,{"derivedFrom":makeQuery(id+"F2.opSweep","SWEPT_EDGE",EDGE,{"disambiguationData":[OSD([sQuery(id+"F0.wireOp",EDGE,"E3"),sQuery(id+"F0.wireOp",EDGE,"E6"),sQuery(id+"F1.wireOp",EDGE,"E9.filletArc")])]}),"instanceName":"2"});
            var Q148;
            Q148=makeQuery(id+"F4.opPattern","COPY",EDGE,{"derivedFrom":makeQuery(id+"F2.opSweep","MID_CAP_EDGE",EDGE,{"disambiguationData":[OSD([sQuery(id+"F0.wireOp",EDGE,"E6"),sQuery(id+"F1.wireOp",VERTEX,"E9.filletArc.end")])],"capPos":1.0}),"instanceName":"2"});
            var Q149;
            Q149=makeQuery(id+"F2.opSweep","SWEPT_EDGE",EDGE,{"disambiguationData":[OSD([sQuery(id+"F0.wireOp",EDGE,"E2"),sQuery(id+"F0.wireOp",EDGE,"E5"),sQuery(id+"F1.wireOp",EDGE,"E8")])]});
            var Q150;
            Q150=makeQuery(id+"F2.opSweep","SWEPT_EDGE",EDGE,{"disambiguationData":[OSD([sQuery(id+"F0.wireOp",EDGE,"E2"),sQuery(id+"F0.wireOp",EDGE,"E5"),sQuery(id+"F1.wireOp",EDGE,"E7")])]});
            var Q151;
            Q151=makeQuery(id+"F2.opSweep","SWEPT_EDGE",EDGE,{"disambiguationData":[OSD([sQuery(id+"F0.wireOp",EDGE,"E2"),sQuery(id+"F0.wireOp",EDGE,"E5"),sQuery(id+"F1.wireOp",EDGE,"E9.filletArc")])]});
            var Q152;
            Q152=makeQuery(id+"F2.opSweep","SWEPT_EDGE",EDGE,{"disambiguationData":[OSD([sQuery(id+"F0.wireOp",EDGE,"E2"),sQuery(id+"F0.wireOp",EDGE,"E6"),sQuery(id+"F1.wireOp",EDGE,"E9.filletArc")])]});
            var Q153;
            Q153=makeQuery(id+"F2.opSweep","SWEPT_EDGE",EDGE,{"disambiguationData":[OSD([sQuery(id+"F0.wireOp",EDGE,"E2"),sQuery(id+"F0.wireOp",EDGE,"E6"),sQuery(id+"F1.wireOp",EDGE,"E8")])]});
            var Q154;
            Q154=makeQuery(id+"F2.opSweep","SWEPT_EDGE",EDGE,{"disambiguationData":[OSD([sQuery(id+"F0.wireOp",EDGE,"E3"),sQuery(id+"F0.wireOp",EDGE,"E5"),sQuery(id+"F1.wireOp",EDGE,"E8")])]});
            var Q155;
            Q155=makeQuery(id+"F2.opSweep","SWEPT_EDGE",EDGE,{"disambiguationData":[OSD([sQuery(id+"F0.wireOp",EDGE,"E3"),sQuery(id+"F0.wireOp",EDGE,"E5"),sQuery(id+"F1.wireOp",EDGE,"E7")])]});
            var Q156;
            Q156=makeQuery(id+"F2.opSweep","CAP_EDGE",EDGE,{"disambiguationData":[OSD([sQuery(id+"F0.wireOp",EDGE,"E2"),sQuery(id+"F1.wireOp",VERTEX,"E8.start")])],"isStart":false});
            var Q157;
            Q157=makeQuery(id+"F2.opSweep","MID_CAP_EDGE",EDGE,{"disambiguationData":[OSD([sQuery(id+"F0.wireOp",EDGE,"E2"),sQuery(id+"F1.wireOp",VERTEX,"E8.end")])],"capPos":2.0});
            var Q158;
            Q158=makeQuery(id+"F2.opSweep","MID_CAP_EDGE",EDGE,{"disambiguationData":[OSD([sQuery(id+"F0.wireOp",EDGE,"E2"),sQuery(id+"F1.wireOp",VERTEX,"E9.filletArc.end")])],"capPos":1.0});
            var Q159;
            Q159=makeQuery(id+"F2.opSweep","CAP_EDGE",EDGE,{"disambiguationData":[OSD([sQuery(id+"F0.wireOp",EDGE,"E3"),sQuery(id+"F1.wireOp",VERTEX,"E8.start")])],"isStart":false});
            var Q160;
            Q160=makeQuery(id+"F2.opSweep","CAP_EDGE",EDGE,{"disambiguationData":[OSD([sQuery(id+"F0.wireOp",EDGE,"E5"),sQuery(id+"F1.wireOp",VERTEX,"E8.start")])],"isStart":false});
            var Q161;
            Q161=makeQuery(id+"F2.opSweep","MID_CAP_EDGE",EDGE,{"disambiguationData":[OSD([sQuery(id+"F0.wireOp",EDGE,"E5"),sQuery(id+"F1.wireOp",VERTEX,"E9.filletArc.end")])],"capPos":1.0});
            var Q162;
            Q162=makeQuery(id+"F2.opSweep","MID_CAP_EDGE",EDGE,{"disambiguationData":[OSD([sQuery(id+"F0.wireOp",EDGE,"E6"),sQuery(id+"F1.wireOp",VERTEX,"E8.end")])],"capPos":2.0});
            var Q163;
            Q163=makeQuery(id+"F4.opPattern","COPY",EDGE,{"derivedFrom":makeQuery(id+"F2.opSweep","MID_CAP_EDGE",EDGE,{"disambiguationData":[OSD([sQuery(id+"F0.wireOp",EDGE,"E5"),sQuery(id+"F1.wireOp",VERTEX,"E9.filletArc.end")])],"capPos":1.0}),"instanceName":"3"});
            var Q164;
            Q164=makeQuery(id+"F4.opPattern","COPY",EDGE,{"derivedFrom":makeQuery(id+"F2.opSweep","SWEPT_EDGE",EDGE,{"disambiguationData":[OSD([sQuery(id+"F0.wireOp",EDGE,"E3"),sQuery(id+"F0.wireOp",EDGE,"E5"),sQuery(id+"F1.wireOp",EDGE,"E9.filletArc")])]}),"instanceName":"3"});
            var Q165;
            Q165=makeQuery(id+"F4.opPattern","COPY",EDGE,{"derivedFrom":makeQuery(id+"F2.opSweep","MID_CAP_EDGE",EDGE,{"disambiguationData":[OSD([sQuery(id+"F0.wireOp",EDGE,"E6"),sQuery(id+"F1.wireOp",VERTEX,"E8.end")])],"capPos":2.0}),"instanceName":"3"});
            var Q166;
            Q166=makeQuery(id+"F4.opPattern","COPY",EDGE,{"derivedFrom":makeQuery(id+"F2.opSweep","SWEPT_EDGE",EDGE,{"disambiguationData":[OSD([sQuery(id+"F0.wireOp",EDGE,"E3"),sQuery(id+"F0.wireOp",EDGE,"E6"),sQuery(id+"F1.wireOp",EDGE,"E9.filletArc")])]}),"instanceName":"3"});
            var Q167;
            Q167=makeQuery(id+"F4.opPattern","COPY",EDGE,{"derivedFrom":makeQuery(id+"F2.opSweep","MID_CAP_EDGE",EDGE,{"disambiguationData":[OSD([sQuery(id+"F0.wireOp",EDGE,"E6"),sQuery(id+"F1.wireOp",VERTEX,"E9.filletArc.end")])],"capPos":1.0}),"instanceName":"3"});
            var Q168;
            Q168=makeQuery(id+"F4.opPattern","COPY",EDGE,{"derivedFrom":makeQuery(id+"F2.opSweep","SWEPT_EDGE",EDGE,{"disambiguationData":[OSD([sQuery(id+"F0.wireOp",EDGE,"E2"),sQuery(id+"F0.wireOp",EDGE,"E6"),sQuery(id+"F1.wireOp",EDGE,"E9.filletArc")])]}),"instanceName":"3"});
            var Q169;
            Q169=makeQuery(id+"F4.opPattern","COPY",EDGE,{"derivedFrom":makeQuery(id+"F2.opSweep","MID_CAP_EDGE",EDGE,{"disambiguationData":[OSD([sQuery(id+"F0.wireOp",EDGE,"E3"),sQuery(id+"F1.wireOp",VERTEX,"E8.end")])],"capPos":2.0}),"instanceName":"3"});
            var Q170;
            Q170=makeQuery(id+"F4.opPattern","COPY",EDGE,{"derivedFrom":makeQuery(id+"F2.opSweep","MID_CAP_EDGE",EDGE,{"disambiguationData":[OSD([sQuery(id+"F0.wireOp",EDGE,"E3"),sQuery(id+"F1.wireOp",VERTEX,"E9.filletArc.end")])],"capPos":1.0}),"instanceName":"3"});
            var Q171;
            Q171=makeQuery(id+"F2.opSweep","MID_CAP_EDGE",EDGE,{"disambiguationData":[OSD([sQuery(id+"F0.wireOp",EDGE,"E5"),sQuery(id+"F1.wireOp",VERTEX,"E8.end")])],"capPos":2.0});
            var Q172;
            Q172=makeQuery(id+"F2.opSweep","CAP_EDGE",EDGE,{"disambiguationData":[OSD([sQuery(id+"F0.wireOp",EDGE,"E6"),sQuery(id+"F1.wireOp",VERTEX,"E8.start")])],"isStart":false});
            fillet(context, id + "F7", {"entities" : qUnion([Q0, Q1, Q2, Q3, Q4, Q5, Q6, Q7, Q8, Q9, Q10, Q11, Q12, Q13, Q14, Q15, Q16, Q17, Q18, Q19, Q20, Q21, Q22, Q23, Q24, Q25, Q26, Q27, Q28, Q29, Q30, Q31, Q32, Q33, Q34, Q35, Q36, Q37, Q38, Q39, Q40, Q41, Q42, Q43, Q44, Q45, Q46, Q47, Q48, Q49, Q50, Q51, Q52, Q53, Q54, Q55, Q56, Q57, Q58, Q59, Q60, Q61, Q62, Q63, Q64, Q65, Q66, Q67, Q68, Q69, Q70, Q71, Q72, Q73, Q74, Q75, Q76, Q77, Q78, Q79, Q80, Q81, Q82, Q83, Q84, Q85, Q86, Q87, Q88, Q89, Q90, Q91, Q92, Q93, Q94, Q95, Q96, Q97, Q98, Q99, Q100, Q101, Q102, Q103, Q104, Q105, Q106, Q107, Q108, Q109, Q110, Q111, Q112, Q113, Q114, Q115, Q116, Q117, Q118, Q119, Q120, Q121, Q122, Q123, Q124, Q125, Q126, Q127, Q128, Q129, Q130, Q131, Q132, Q133, Q134, Q135, Q136, Q137, Q138, Q139, Q140, Q141, Q142, Q143, Q144, Q145, Q146, Q147, Q148, Q149, Q150, Q151, Q152, Q153, Q154, Q155, Q156, Q157, Q158, Q159, Q160, Q161, Q162, Q163, Q164, Q165, Q166, Q167, Q168, Q169, Q170, Q171, Q172]), "radius" : 3 * mm, "tangentPropagation" : true, "allowEdgeOverflow" : false});
        }
    });
